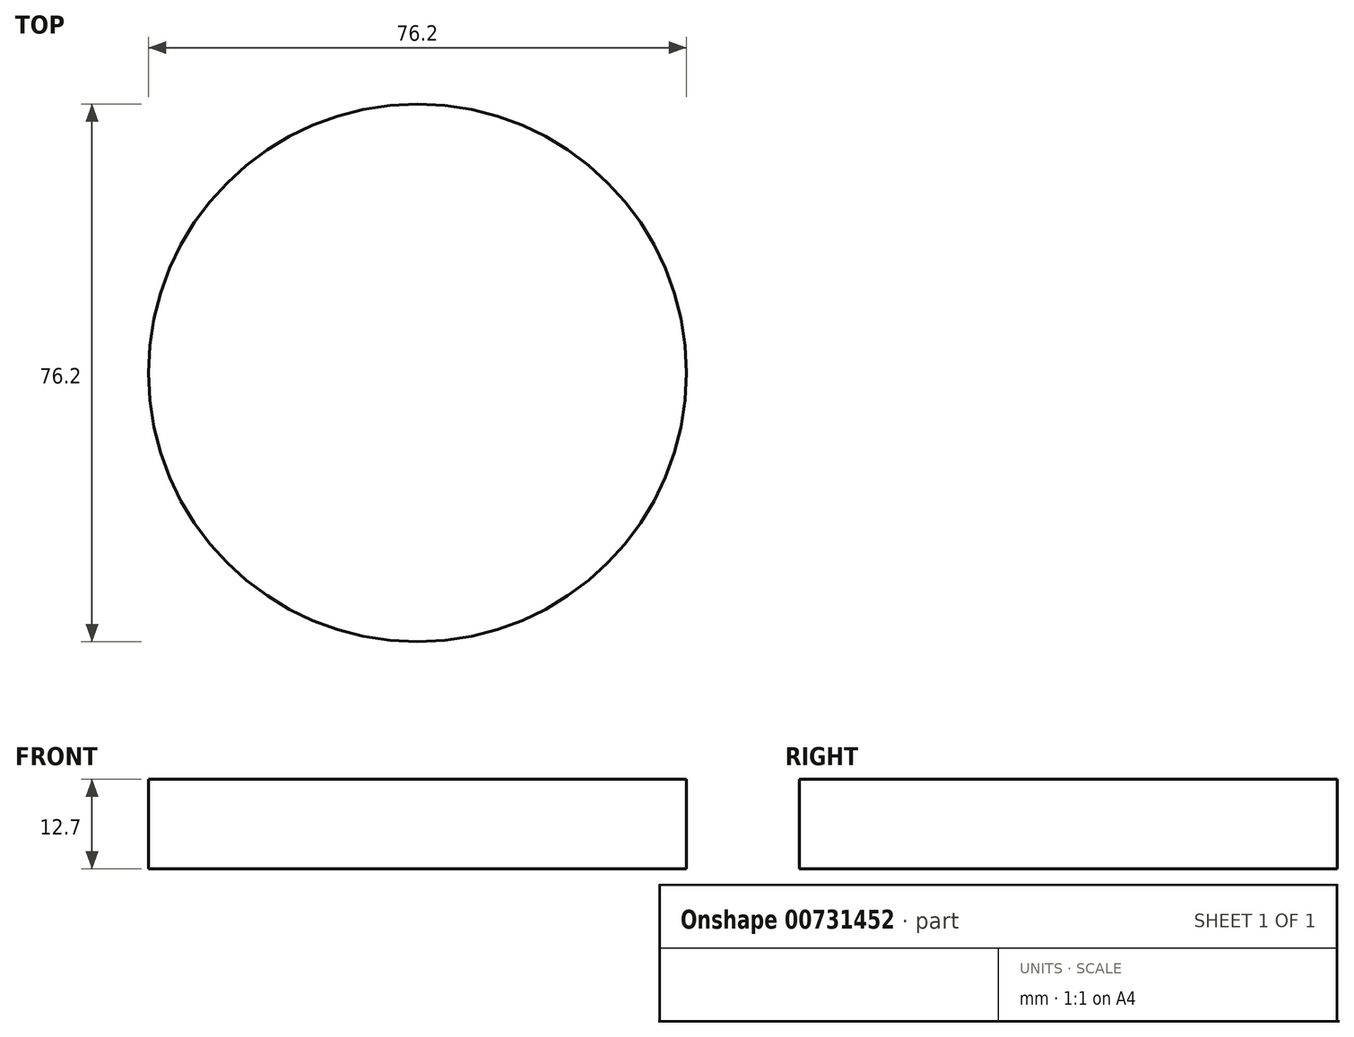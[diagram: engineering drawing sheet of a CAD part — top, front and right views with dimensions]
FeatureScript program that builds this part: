
annotation { "Feature Type Name" : "Feature", "Feature Type Description" : "" }
export const myFeature = defineFeature(function(context is Context, id is Id, definition is map)
    precondition{}
    {
        {
            var Q0;
            Q0=qCreatedBy(makeId("Top.planeOp"),FACE);
            var sketch = newSketch(context, id + "F0", { "sketchPlane" : qUnion([Q0])});
            skCircle(sketch, "E0", {"center": v(0, 0) * mm, "radius": 38.1 * mm});
            skCircle(sketch, "E1", {"center": v(0, 0) * mm, "radius": 28.58 * mm});
            skSolve(sketch);
        }
        {
            var Q0;
            Q0=makeQuery(id+"F0.imprint","IMPRINT",FACE,{"disambiguationData":[TD([[makeQuery(id+"F0.imprint","IMPRINT",EDGE,{"derivedFrom":sQuery(id+"F0.wireOp",EDGE,"E0")}),1.0]])]});
            var Q1;
            Q1=makeQuery(id+"F0.imprint","IMPRINT",FACE,{"disambiguationData":[TD([[makeQuery(id+"F0.imprint","IMPRINT",EDGE,{"derivedFrom":sQuery(id+"F0.wireOp",EDGE,"E1")}),1.0]])]});
            extrude(context, id + "F1", {"entities" : qUnion([Q0, Q1]), "depth" : 12.7 * mm, "offsetDistance" : 25.4 * mm});
        }
    });
